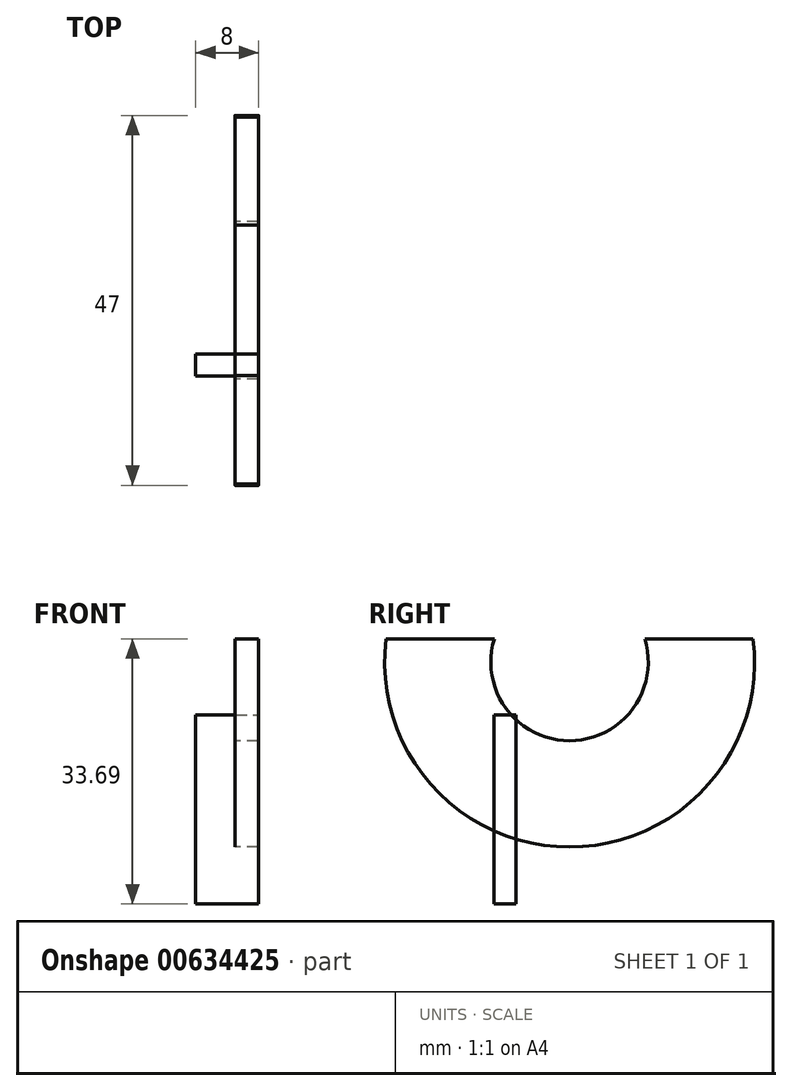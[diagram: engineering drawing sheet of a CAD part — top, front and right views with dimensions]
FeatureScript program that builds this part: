
annotation { "Feature Type Name" : "Feature", "Feature Type Description" : "" }
export const myFeature = defineFeature(function(context is Context, id is Id, definition is map)
    precondition{}
    {
        {
            assignVariable(context, id + "F0", {"name" : "ShelfThick", "anyValue" : 5 * mm});
        }
        {
            var Q0;
            Q0=qCreatedBy(makeId("Right.planeOp"),FACE);
            var sketch = newSketch(context, id + "F1", { "sketchPlane" : qUnion([Q0])});
            skLineSegment(sketch, "E0.bottom", {"start": v(0, 0) * mm, "end": v(203.2, 0) * mm});
            skLineSegment(sketch, "E0.top", {"start": v(0, 5) * mm, "end": v(203.2, 5) * mm});
            skLineSegment(sketch, "E0.left", {"start": v(0, 0) * mm, "end": v(0, 5) * mm});
            skLineSegment(sketch, "E0.right", {"start": v(203.2, 0) * mm, "end": v(203.2, 5) * mm});
            skLineSegment(sketch, "E1.bottom", {"start": v(0, 0) * mm, "end": v(5, 0) * mm});
            skLineSegment(sketch, "E1.top", {"start": v(0, -95) * mm, "end": v(5, -95) * mm});
            skLineSegment(sketch, "E1.left", {"start": v(0, 0) * mm, "end": v(0, -95) * mm});
            skLineSegment(sketch, "E1.right", {"start": v(5, 0) * mm, "end": v(5, -95) * mm});
            skSolve(sketch);
        }
        {
            assignVariable(context, id + "F2", {"name" : "BracketThick", "anyValue" : 3 * mm});
        }
        {
            var Q0;
            Q0=qCreatedBy(makeId("Right.planeOp"),FACE);
            var sketch = newSketch(context, id + "F3", { "sketchPlane" : qUnion([Q0])});
            skCircle(sketch, "E2", {"center": v(9.58, -2.85) * mm, "radius": 10 * mm});
            skCircle(sketch, "E3.0", {"center": v(9.58, -2.85) * mm, "radius": 23.5 * mm});
            skLineSegment(sketch, "E4", {"start": v(32.9, 0.09) * mm, "end": v(-13.74, 0.09) * mm});
            skLineSegment(sketch, "E5.bottom", {"start": v(2.75, -9.6) * mm, "end": v(0, -9.6) * mm});
            skLineSegment(sketch, "E5.top", {"start": v(2.75, -33.6) * mm, "end": v(0, -33.6) * mm});
            skLineSegment(sketch, "E5.left", {"start": v(2.75, -9.6) * mm, "end": v(2.75, -33.6) * mm});
            skLineSegment(sketch, "E5.right", {"start": v(0, -9.6) * mm, "end": v(0, -33.6) * mm});
            skLineSegment(sketch, "E6.bottom", {"start": v(23.11, 0.09) * mm, "end": v(28.11, 0.09) * mm});
            skLineSegment(sketch, "E6.top", {"start": v(23.11, 8.09) * mm, "end": v(28.11, 8.09) * mm});
            skLineSegment(sketch, "E6.left", {"start": v(23.11, 0.09) * mm, "end": v(23.11, 8.09) * mm});
            skLineSegment(sketch, "E6.right", {"start": v(28.11, 0.09) * mm, "end": v(28.11, 8.09) * mm});
            skSolve(sketch);
        }
        {
            var Q0;
            {var subQ0=sQuery(id+"F3.wireOp",EDGE,"E4");var subQ1=sQuery(id+"F3.wireOp",EDGE,"E2");var subQ2=makeQuery(id+"F3.imprint","INTERSECT",VERTEX,{"disambiguationData":[OD(1.0)],"derivedFrom":[subQ1,subQ0]});Q0=makeQuery(id+"F3.imprint","IMPRINT",FACE,{"disambiguationData":[TD([[makeQuery(id+"F3.imprint","IMPRINT",EDGE,{"disambiguationData":[TD([[subQ2,1.0]])],"derivedFrom":subQ1}),-1.0]])]});}
            var Q1;
            {var subQ3=sQuery(id+"F3.wireOp",EDGE,"E2");var subQ5=sQuery(id+"F3.wireOp",EDGE,"E4");var subQ6=makeQuery(id+"F3.imprint","INTERSECT",VERTEX,{"disambiguationData":[OD(0.0)],"derivedFrom":[subQ3,subQ5]});Q1=makeQuery(id+"F3.imprint","IMPRINT",FACE,{"disambiguationData":[TD([[makeQuery(id+"F3.imprint","IMPRINT",EDGE,{"disambiguationData":[TD([[subQ6,-1.0]])],"derivedFrom":subQ3}),-1.0]])]});}
            var Q2;
            {var subQ3=sQuery(id+"F3.wireOp",EDGE,"E2");var subQ7=sQuery(id+"F3.wireOp",EDGE,"E5.bottom");var subQ9=makeQuery(id+"F3.imprint","INTERSECT",VERTEX,{"derivedFrom":[subQ3,subQ7]});Q2=makeQuery(id+"F3.imprint","IMPRINT",FACE,{"disambiguationData":[TD([[makeQuery(id+"F3.imprint","IMPRINT",EDGE,{"disambiguationData":[TD([[subQ9,-1.0]])],"derivedFrom":subQ3}),-1.0]])]});}
            var Q3;
            Q3=makeQuery(id+"F3.imprint","IMPRINT",FACE,{"disambiguationData":[TD([[makeQuery(id+"F3.imprint","IMPRINT",EDGE,{"derivedFrom":sQuery(id+"F3.wireOp",EDGE,"E6.bottom")}),1.0]])]});
            extrude(context, id + "F4", {"entities" : qUnion([Q0, Q1, Q2, Q3]), "depth" : getVariable(context, 'BracketThick'), "offsetDistance" : 25 * mm});
        }
        {
            var Q0;
            {var subQ0=sQuery(id+"F3.wireOp",EDGE,"E5.bottom");var subQ1=sQuery(id+"F3.wireOp",EDGE,"E2");var subQ2=makeQuery(id+"F3.imprint","INTERSECT",VERTEX,{"derivedFrom":[subQ1,subQ0]});Q0=makeQuery(id+"F3.imprint","IMPRINT",FACE,{"disambiguationData":[TD([[makeQuery(id+"F3.imprint","IMPRINT",EDGE,{"disambiguationData":[TD([[subQ2,-1.0]])],"derivedFrom":subQ1}),1.0]])]});}
            var Q1;
            {var subQ3=sQuery(id+"F3.wireOp",EDGE,"E2");var subQ7=sQuery(id+"F3.wireOp",EDGE,"E5.bottom");var subQ9=makeQuery(id+"F3.imprint","INTERSECT",VERTEX,{"derivedFrom":[subQ3,subQ7]});Q1=makeQuery(id+"F3.imprint","IMPRINT",FACE,{"disambiguationData":[TD([[makeQuery(id+"F3.imprint","IMPRINT",EDGE,{"disambiguationData":[TD([[subQ9,-1.0]])],"derivedFrom":subQ3}),-1.0]])]});}
            var Q2;
            {var subQ5=sQuery(id+"F3.wireOp",EDGE,"E5.top");Q2=makeQuery(id+"F3.imprint","IMPRINT",FACE,{"disambiguationData":[TD([[makeQuery(id+"F3.imprint","IMPRINT",EDGE,{"derivedFrom":subQ5}),-1.0]])]});}
            extrude(context, id + "F5", {"entities" : qUnion([Q0, Q1, Q2]), "oppositeDirection" : true, "depth" : getVariable(context, 'ShelfThick'), "offsetDistance" : 25 * mm, "hasSecondDirection" : true, "secondDirectionOppositeDirection" : false, "secondDirectionDepth" : getVariable(context, 'BracketThick')});
        }
    });
